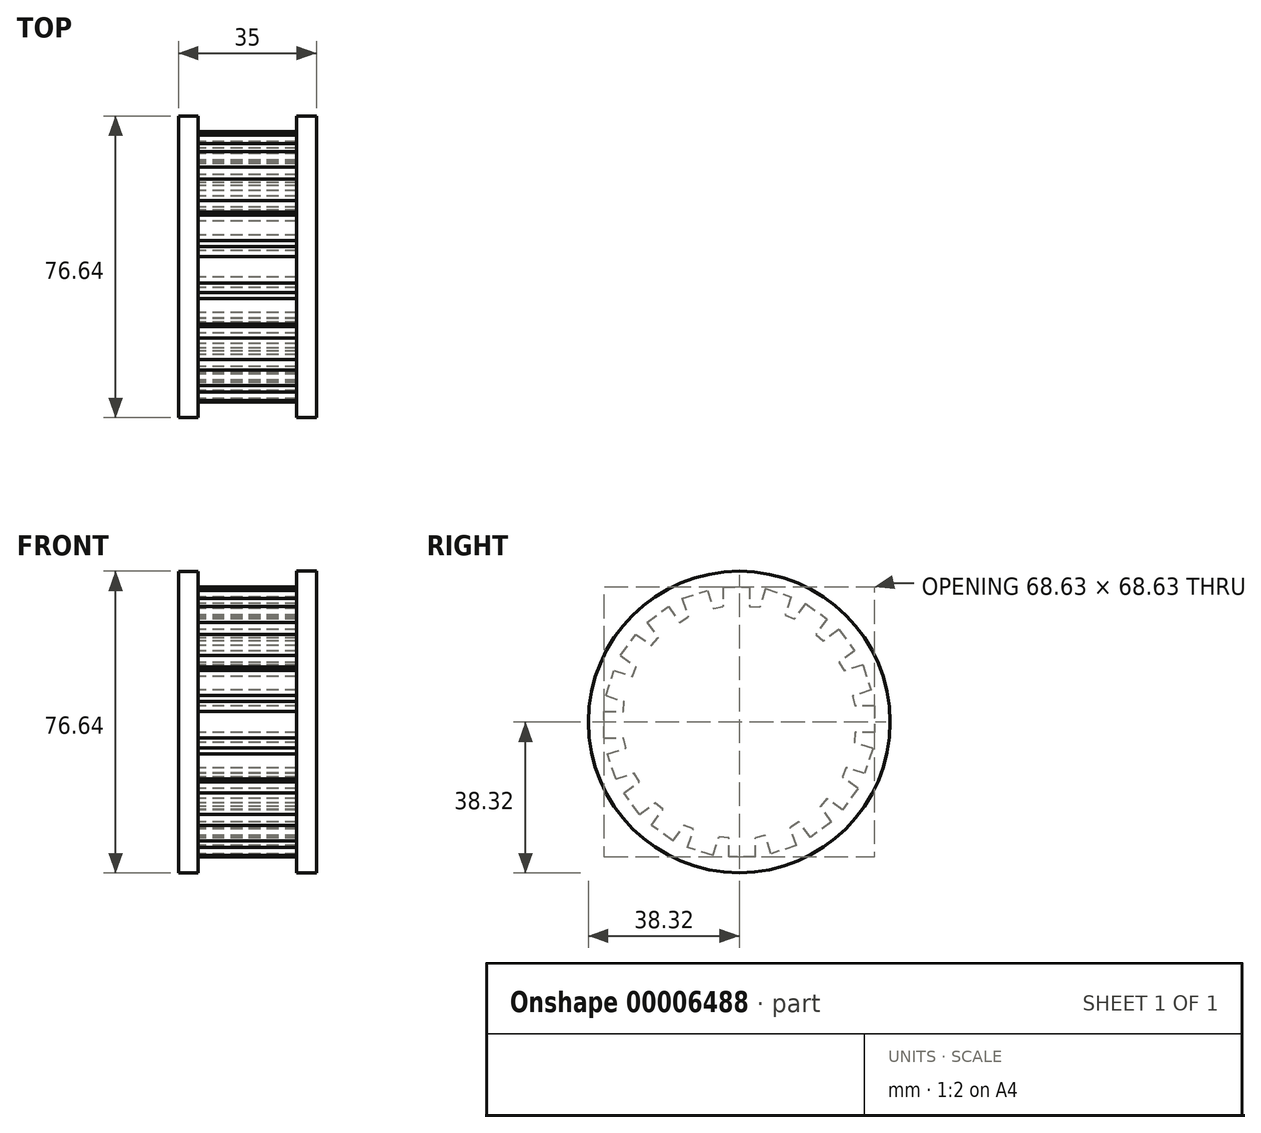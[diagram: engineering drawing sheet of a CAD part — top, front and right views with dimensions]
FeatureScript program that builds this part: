
annotation { "Feature Type Name" : "Feature", "Feature Type Description" : "" }
export const myFeature = defineFeature(function(context is Context, id is Id, definition is map)
    precondition{}
    {
        {
            var Q0;
            Q0=qCreatedBy(makeId("Right.planeOp"),FACE);
            var sketch = newSketch(context, id + "F0", { "sketchPlane" : qUnion([Q0])});
            skCircle(sketch, "E0", {"center": v(0, 0) * mm, "radius": 38.27 * mm});
            skSolve(sketch);
        }
        {
            var Q0;
            Q0=makeQuery(id+"F0.imprint","IMPRINT",FACE,{"disambiguationData":[TD([[makeQuery(id+"F0.imprint","IMPRINT",EDGE,{"derivedFrom":sQuery(id+"F0.wireOp",EDGE,"E0")}),1.0]])]});
            extrude(context, id + "F1", {"entities" : qUnion([Q0]), "depth" : 5 * mm});
        }
        {
            var Q0;
            Q0=makeQuery(id+"F1.opExtrude","CAP_FACE",FACE,{"disambiguationData":[OSD([sQuery(id+"F0.wireOp",EDGE,"E0")])],"isStart":false});
            var sketch = newSketch(context, id + "F2", { "sketchPlane" : qUnion([Q0])});
            skLineSegment(sketch, "E1.bottom", {"start": v(-4.09, 34.32) * mm, "end": v(2.64, 34.32) * mm});
            skLineSegment(sketch, "E1.left", {"start": v(-4.09, 34.32) * mm, "end": v(-4.09, 29.42) * mm});
            skLineSegment(sketch, "E1.right", {"start": v(2.64, 34.32) * mm, "end": v(2.64, 29.42) * mm});
            skLineSegment(sketch, "E2.1.0", {"start": v(-8.1, 33.45) * mm, "end": v(-6.58, 28.8) * mm});
            skLineSegment(sketch, "E2.1.1", {"start": v(-14.5, 31.37) * mm, "end": v(-12.98, 26.72) * mm});
            skLineSegment(sketch, "E2.1.3", {"start": v(-14.5, 31.37) * mm, "end": v(-8.1, 33.45) * mm});
            skLineSegment(sketch, "E2.2.0", {"start": v(-18.03, 29.31) * mm, "end": v(-15.16, 25.35) * mm});
            skLineSegment(sketch, "E2.2.1", {"start": v(-23.48, 25.36) * mm, "end": v(-20.6, 21.4) * mm});
            skLineSegment(sketch, "E2.2.3", {"start": v(-23.48, 25.36) * mm, "end": v(-18.03, 29.31) * mm});
            skPoint(sketch, "E2.center", {"position": v(0, 0) * mm});
            skLineSegment(sketch, "E3.2.3.0", {"start": v(-26.2, 22.3) * mm, "end": v(-22.25, 19.43) * mm});
            skLineSegment(sketch, "E3.3.3.0", {"start": v(-30.16, 16.86) * mm, "end": v(-26.2, 13.99) * mm});
            skLineSegment(sketch, "E3.9.3.0", {"start": v(-30.16, 16.86) * mm, "end": v(-26.2, 22.3) * mm});
            skLineSegment(sketch, "E3.2.4.0", {"start": v(-31.82, 13.12) * mm, "end": v(-27.16, 11.6) * mm});
            skLineSegment(sketch, "E3.3.4.0", {"start": v(-33.9, 6.72) * mm, "end": v(-29.24, 5.2) * mm});
            skLineSegment(sketch, "E3.9.4.0", {"start": v(-33.9, 6.72) * mm, "end": v(-31.82, 13.12) * mm});
            skLineSegment(sketch, "E3.2.5.0", {"start": v(-34.32, 2.64) * mm, "end": v(-29.42, 2.64) * mm});
            skLineSegment(sketch, "E3.3.5.0", {"start": v(-34.32, -4.09) * mm, "end": v(-29.42, -4.09) * mm});
            skLineSegment(sketch, "E3.9.5.0", {"start": v(-34.32, -4.09) * mm, "end": v(-34.32, 2.64) * mm});
            skLineSegment(sketch, "E3.2.6.0", {"start": v(-33.45, -8.1) * mm, "end": v(-28.8, -6.58) * mm});
            skLineSegment(sketch, "E3.3.6.0", {"start": v(-31.37, -14.5) * mm, "end": v(-26.72, -12.98) * mm});
            skLineSegment(sketch, "E3.9.6.0", {"start": v(-31.37, -14.5) * mm, "end": v(-33.45, -8.1) * mm});
            skLineSegment(sketch, "E3.2.7.0", {"start": v(-29.31, -18.03) * mm, "end": v(-25.35, -15.16) * mm});
            skLineSegment(sketch, "E3.3.7.0", {"start": v(-25.36, -23.48) * mm, "end": v(-21.4, -20.6) * mm});
            skLineSegment(sketch, "E3.9.7.0", {"start": v(-25.36, -23.48) * mm, "end": v(-29.31, -18.03) * mm});
            skLineSegment(sketch, "E3.2.8.0", {"start": v(-22.3, -26.2) * mm, "end": v(-19.43, -22.25) * mm});
            skLineSegment(sketch, "E3.3.8.0", {"start": v(-16.86, -30.16) * mm, "end": v(-13.99, -26.2) * mm});
            skLineSegment(sketch, "E3.9.8.0", {"start": v(-16.86, -30.16) * mm, "end": v(-22.3, -26.2) * mm});
            skLineSegment(sketch, "E3.2.9.0", {"start": v(-13.12, -31.82) * mm, "end": v(-11.6, -27.16) * mm});
            skLineSegment(sketch, "E3.3.9.0", {"start": v(-6.72, -33.9) * mm, "end": v(-5.2, -29.24) * mm});
            skLineSegment(sketch, "E3.9.9.0", {"start": v(-6.72, -33.9) * mm, "end": v(-13.12, -31.82) * mm});
            skLineSegment(sketch, "E3.2.10.0", {"start": v(-2.64, -34.32) * mm, "end": v(-2.64, -29.42) * mm});
            skLineSegment(sketch, "E3.3.10.0", {"start": v(4.09, -34.32) * mm, "end": v(4.09, -29.42) * mm});
            skLineSegment(sketch, "E3.9.10.0", {"start": v(4.09, -34.32) * mm, "end": v(-2.64, -34.32) * mm});
            skLineSegment(sketch, "E3.2.11.0", {"start": v(8.1, -33.45) * mm, "end": v(6.58, -28.8) * mm});
            skLineSegment(sketch, "E3.3.11.0", {"start": v(14.5, -31.37) * mm, "end": v(12.98, -26.72) * mm});
            skLineSegment(sketch, "E3.9.11.0", {"start": v(14.5, -31.37) * mm, "end": v(8.1, -33.45) * mm});
            skLineSegment(sketch, "E3.2.12.0", {"start": v(18.03, -29.31) * mm, "end": v(15.16, -25.35) * mm});
            skLineSegment(sketch, "E3.3.12.0", {"start": v(23.48, -25.36) * mm, "end": v(20.6, -21.4) * mm});
            skLineSegment(sketch, "E3.9.12.0", {"start": v(23.48, -25.36) * mm, "end": v(18.03, -29.31) * mm});
            skLineSegment(sketch, "E3.2.13.0", {"start": v(26.2, -22.3) * mm, "end": v(22.25, -19.43) * mm});
            skLineSegment(sketch, "E3.3.13.0", {"start": v(30.16, -16.86) * mm, "end": v(26.2, -13.99) * mm});
            skLineSegment(sketch, "E3.9.13.0", {"start": v(30.16, -16.86) * mm, "end": v(26.2, -22.3) * mm});
            skLineSegment(sketch, "E3.2.14.0", {"start": v(31.82, -13.12) * mm, "end": v(27.16, -11.6) * mm});
            skLineSegment(sketch, "E3.3.14.0", {"start": v(33.9, -6.72) * mm, "end": v(29.24, -5.2) * mm});
            skLineSegment(sketch, "E3.9.14.0", {"start": v(33.9, -6.72) * mm, "end": v(31.82, -13.12) * mm});
            skLineSegment(sketch, "E3.2.15.0", {"start": v(34.32, -2.64) * mm, "end": v(29.42, -2.64) * mm});
            skLineSegment(sketch, "E3.3.15.0", {"start": v(34.32, 4.09) * mm, "end": v(29.42, 4.09) * mm});
            skLineSegment(sketch, "E3.9.15.0", {"start": v(34.32, 4.09) * mm, "end": v(34.32, -2.64) * mm});
            skLineSegment(sketch, "E3.2.16.0", {"start": v(33.45, 8.1) * mm, "end": v(28.8, 6.58) * mm});
            skLineSegment(sketch, "E3.3.16.0", {"start": v(31.37, 14.5) * mm, "end": v(26.72, 12.98) * mm});
            skLineSegment(sketch, "E3.9.16.0", {"start": v(31.37, 14.5) * mm, "end": v(33.45, 8.1) * mm});
            skLineSegment(sketch, "E3.2.17.0", {"start": v(29.31, 18.03) * mm, "end": v(25.35, 15.16) * mm});
            skLineSegment(sketch, "E3.3.17.0", {"start": v(25.36, 23.48) * mm, "end": v(21.4, 20.6) * mm});
            skLineSegment(sketch, "E3.9.17.0", {"start": v(25.36, 23.48) * mm, "end": v(29.31, 18.03) * mm});
            skLineSegment(sketch, "E3.2.18.0", {"start": v(22.3, 26.2) * mm, "end": v(19.43, 22.25) * mm});
            skLineSegment(sketch, "E3.3.18.0", {"start": v(16.86, 30.16) * mm, "end": v(13.99, 26.2) * mm});
            skLineSegment(sketch, "E3.9.18.0", {"start": v(16.86, 30.16) * mm, "end": v(22.3, 26.2) * mm});
            skLineSegment(sketch, "E3.2.19.0", {"start": v(13.12, 31.82) * mm, "end": v(11.6, 27.16) * mm});
            skLineSegment(sketch, "E3.3.19.0", {"start": v(6.72, 33.9) * mm, "end": v(5.2, 29.24) * mm});
            skLineSegment(sketch, "E3.9.19.0", {"start": v(6.72, 33.9) * mm, "end": v(13.12, 31.82) * mm});
            skLineSegment(sketch, "E4", {"start": v(-29.42, 2.64) * mm, "end": v(-29.24, 5.2) * mm});
            skLineSegment(sketch, "E5", {"start": v(-27.16, 11.6) * mm, "end": v(-26.2, 13.99) * mm});
            skLineSegment(sketch, "E6", {"start": v(-22.25, 19.43) * mm, "end": v(-20.6, 21.4) * mm});
            skLineSegment(sketch, "E7", {"start": v(-15.16, 25.35) * mm, "end": v(-12.98, 26.72) * mm});
            skLineSegment(sketch, "E8", {"start": v(-6.58, 28.8) * mm, "end": v(-4.09, 29.42) * mm});
            skLineSegment(sketch, "E9", {"start": v(2.64, 29.42) * mm, "end": v(5.2, 29.24) * mm});
            skLineSegment(sketch, "E10", {"start": v(11.6, 27.16) * mm, "end": v(13.99, 26.2) * mm});
            skLineSegment(sketch, "E11", {"start": v(19.43, 22.25) * mm, "end": v(21.4, 20.6) * mm});
            skLineSegment(sketch, "E12", {"start": v(25.35, 15.16) * mm, "end": v(26.72, 12.98) * mm});
            skLineSegment(sketch, "E13", {"start": v(28.8, 6.58) * mm, "end": v(29.42, 4.09) * mm});
            skLineSegment(sketch, "E14", {"start": v(29.42, -2.64) * mm, "end": v(29.24, -5.2) * mm});
            skLineSegment(sketch, "E15", {"start": v(27.16, -11.6) * mm, "end": v(26.2, -13.99) * mm});
            skLineSegment(sketch, "E16", {"start": v(22.25, -19.43) * mm, "end": v(20.6, -21.4) * mm});
            skLineSegment(sketch, "E17", {"start": v(15.16, -25.35) * mm, "end": v(12.98, -26.72) * mm});
            skLineSegment(sketch, "E18", {"start": v(6.58, -28.8) * mm, "end": v(4.09, -29.42) * mm});
            skLineSegment(sketch, "E19", {"start": v(-2.64, -29.42) * mm, "end": v(-5.2, -29.24) * mm});
            skLineSegment(sketch, "E20", {"start": v(-11.6, -27.16) * mm, "end": v(-13.99, -26.2) * mm});
            skLineSegment(sketch, "E21", {"start": v(-19.43, -22.25) * mm, "end": v(-21.4, -20.6) * mm});
            skLineSegment(sketch, "E22", {"start": v(-25.35, -15.16) * mm, "end": v(-26.72, -12.98) * mm});
            skLineSegment(sketch, "E23", {"start": v(-28.8, -6.58) * mm, "end": v(-29.42, -4.09) * mm});
            skSolve(sketch);
        }
        {
            var Q0;
            Q0=makeQuery(id+"F2.imprint","IMPRINT",FACE,{"disambiguationData":[TD([[makeQuery(id+"F2.imprint","IMPRINT",EDGE,{"derivedFrom":sQuery(id+"F2.wireOp",EDGE,"E1.bottom")}),-1.0]])]});
            extrude(context, id + "F3", {"entities" : qUnion([Q0]), "operationType" : NewBodyOperationType.ADD, "depth" : 25 * mm});
        }
        {
            var Q0;
            Q0=makeQuery(id+"F3.opExtrude","CAP_FACE",FACE,{"disambiguationData":[OSD([sQuery(id+"F2.wireOp",EDGE,"E1.bottom"),sQuery(id+"F2.wireOp",EDGE,"E1.left"),sQuery(id+"F2.wireOp",EDGE,"E1.right"),sQuery(id+"F2.wireOp",EDGE,"E2.1.0"),sQuery(id+"F2.wireOp",EDGE,"E2.1.1"),sQuery(id+"F2.wireOp",EDGE,"E2.1.3"),sQuery(id+"F2.wireOp",EDGE,"E2.2.0"),sQuery(id+"F2.wireOp",EDGE,"E2.2.1"),sQuery(id+"F2.wireOp",EDGE,"E2.2.3"),sQuery(id+"F2.wireOp",EDGE,"E3.2.3.0"),sQuery(id+"F2.wireOp",EDGE,"E3.3.3.0"),sQuery(id+"F2.wireOp",EDGE,"E3.9.3.0"),sQuery(id+"F2.wireOp",EDGE,"E3.2.4.0"),sQuery(id+"F2.wireOp",EDGE,"E3.3.4.0"),sQuery(id+"F2.wireOp",EDGE,"E3.9.4.0"),sQuery(id+"F2.wireOp",EDGE,"E3.2.5.0"),sQuery(id+"F2.wireOp",EDGE,"E3.3.5.0"),sQuery(id+"F2.wireOp",EDGE,"E3.9.5.0"),sQuery(id+"F2.wireOp",EDGE,"E3.2.6.0"),sQuery(id+"F2.wireOp",EDGE,"E3.3.6.0"),sQuery(id+"F2.wireOp",EDGE,"E3.9.6.0"),sQuery(id+"F2.wireOp",EDGE,"E3.2.7.0"),sQuery(id+"F2.wireOp",EDGE,"E3.3.7.0"),sQuery(id+"F2.wireOp",EDGE,"E3.9.7.0"),sQuery(id+"F2.wireOp",EDGE,"E3.2.8.0"),sQuery(id+"F2.wireOp",EDGE,"E3.3.8.0"),sQuery(id+"F2.wireOp",EDGE,"E3.9.8.0"),sQuery(id+"F2.wireOp",EDGE,"E3.2.9.0"),sQuery(id+"F2.wireOp",EDGE,"E3.3.9.0"),sQuery(id+"F2.wireOp",EDGE,"E3.9.9.0"),sQuery(id+"F2.wireOp",EDGE,"E3.2.10.0"),sQuery(id+"F2.wireOp",EDGE,"E3.3.10.0"),sQuery(id+"F2.wireOp",EDGE,"E3.9.10.0"),sQuery(id+"F2.wireOp",EDGE,"E3.2.11.0"),sQuery(id+"F2.wireOp",EDGE,"E3.3.11.0"),sQuery(id+"F2.wireOp",EDGE,"E3.9.11.0"),sQuery(id+"F2.wireOp",EDGE,"E3.2.12.0"),sQuery(id+"F2.wireOp",EDGE,"E3.3.12.0"),sQuery(id+"F2.wireOp",EDGE,"E3.9.12.0"),sQuery(id+"F2.wireOp",EDGE,"E3.2.13.0"),sQuery(id+"F2.wireOp",EDGE,"E3.3.13.0"),sQuery(id+"F2.wireOp",EDGE,"E3.9.13.0"),sQuery(id+"F2.wireOp",EDGE,"E3.2.14.0"),sQuery(id+"F2.wireOp",EDGE,"E3.3.14.0"),sQuery(id+"F2.wireOp",EDGE,"E3.9.14.0"),sQuery(id+"F2.wireOp",EDGE,"E3.2.15.0"),sQuery(id+"F2.wireOp",EDGE,"E3.3.15.0"),sQuery(id+"F2.wireOp",EDGE,"E3.9.15.0"),sQuery(id+"F2.wireOp",EDGE,"E3.2.16.0"),sQuery(id+"F2.wireOp",EDGE,"E3.3.16.0"),sQuery(id+"F2.wireOp",EDGE,"E3.9.16.0"),sQuery(id+"F2.wireOp",EDGE,"E3.2.17.0"),sQuery(id+"F2.wireOp",EDGE,"E3.3.17.0"),sQuery(id+"F2.wireOp",EDGE,"E3.9.17.0"),sQuery(id+"F2.wireOp",EDGE,"E3.2.18.0"),sQuery(id+"F2.wireOp",EDGE,"E3.3.18.0"),sQuery(id+"F2.wireOp",EDGE,"E3.9.18.0"),sQuery(id+"F2.wireOp",EDGE,"E3.2.19.0"),sQuery(id+"F2.wireOp",EDGE,"E3.3.19.0"),sQuery(id+"F2.wireOp",EDGE,"E3.9.19.0"),sQuery(id+"F2.wireOp",EDGE,"E4"),sQuery(id+"F2.wireOp",EDGE,"E5"),sQuery(id+"F2.wireOp",EDGE,"E6"),sQuery(id+"F2.wireOp",EDGE,"E7"),sQuery(id+"F2.wireOp",EDGE,"E8"),sQuery(id+"F2.wireOp",EDGE,"E9"),sQuery(id+"F2.wireOp",EDGE,"E10"),sQuery(id+"F2.wireOp",EDGE,"E11"),sQuery(id+"F2.wireOp",EDGE,"E12"),sQuery(id+"F2.wireOp",EDGE,"E13"),sQuery(id+"F2.wireOp",EDGE,"E14"),sQuery(id+"F2.wireOp",EDGE,"E15"),sQuery(id+"F2.wireOp",EDGE,"E16"),sQuery(id+"F2.wireOp",EDGE,"E17"),sQuery(id+"F2.wireOp",EDGE,"E18"),sQuery(id+"F2.wireOp",EDGE,"E19"),sQuery(id+"F2.wireOp",EDGE,"E20"),sQuery(id+"F2.wireOp",EDGE,"E21"),sQuery(id+"F2.wireOp",EDGE,"E22"),sQuery(id+"F2.wireOp",EDGE,"E23")])],"isStart":false});
            var sketch = newSketch(context, id + "F4", { "sketchPlane" : qUnion([Q0])});
            skCircle(sketch, "E24", {"center": v(0, 0) * mm, "radius": 38.32 * mm});
            skSolve(sketch);
        }
        {
            var Q0;
            {var subQ21=makeQuery(id+"F4.imprint","IMPRINT",EDGE,{"derivedFrom":makeQuery(id+"F3.opExtrude","CAP_EDGE",EDGE,{"disambiguationData":[OSD([sQuery(id+"F2.wireOp",EDGE,"E1.bottom")])],"isStart":false})});Q0=qUnion([makeQuery(id+"F4.imprint","IMPRINT",FACE,{"disambiguationData":[TD([[makeQuery(id+"F4.imprint","IMPRINT",EDGE,{"derivedFrom":sQuery(id+"F4.wireOp",EDGE,"E24")}),1.0]])]}),makeQuery(id+"F4.imprint","IMPRINT",FACE,{"disambiguationData":[TD([[subQ21,-1.0]])]})]);}
            extrude(context, id + "F5", {"entities" : qUnion([Q0]), "operationType" : NewBodyOperationType.ADD, "depth" : 5 * mm});
        }
    });
